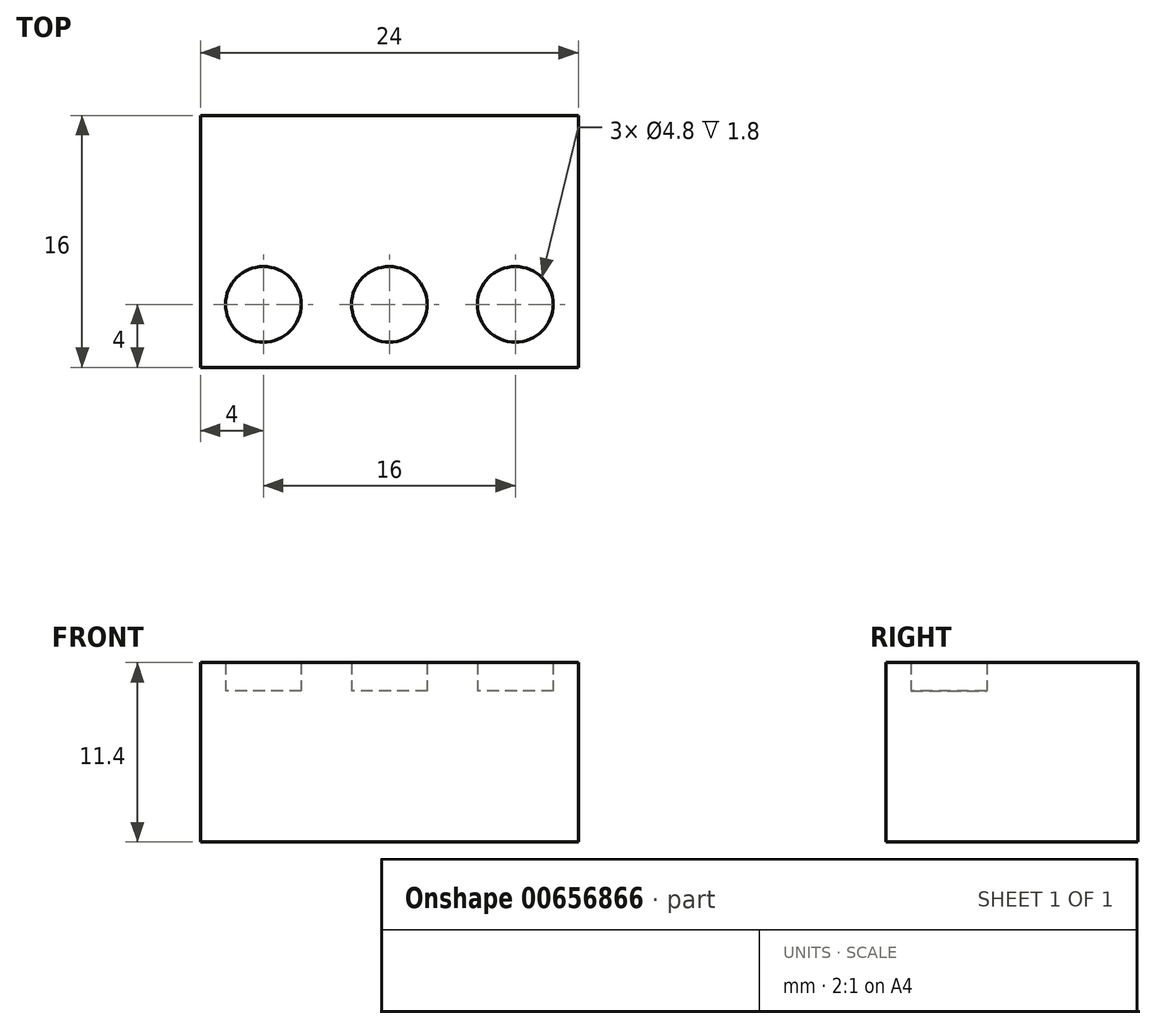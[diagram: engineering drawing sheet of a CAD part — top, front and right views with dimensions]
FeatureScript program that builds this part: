
annotation { "Feature Type Name" : "Feature", "Feature Type Description" : "" }
export const myFeature = defineFeature(function(context is Context, id is Id, definition is map)
    precondition{}
    {
        {
            var Q0;
            Q0=qCreatedBy(makeId("Top.planeOp"),FACE);
            var sketch = newSketch(context, id + "F0", { "sketchPlane" : qUnion([Q0])});
            skLineSegment(sketch, "E0.bottom", {"start": v(0, 0) * mm, "end": v(-24, 0) * mm});
            skLineSegment(sketch, "E0.top", {"start": v(0, 16) * mm, "end": v(-24, 16) * mm});
            skLineSegment(sketch, "E0.left", {"start": v(0, 0) * mm, "end": v(0, 16) * mm});
            skLineSegment(sketch, "E0.right", {"start": v(-24, 0) * mm, "end": v(-24, 16) * mm});
            skSolve(sketch);
        }
        {
            var Q0;
            Q0=makeQuery(id+"F0.imprint","IMPRINT",FACE,{"disambiguationData":[TD([[makeQuery(id+"F0.imprint","IMPRINT",EDGE,{"derivedFrom":sQuery(id+"F0.wireOp",EDGE,"E0.bottom")}),-1.0]])]});
            var Q1;
            Q1 = qSketchRegion(id + "F2", true);
            extrude(context, id + "F1", {"entities" : qUnion([Q0, Q1]), "depth" : 9.6 * mm, "offsetDistance" : 25.4 * mm});
        }
        {
            var Q0;
            Q0=makeQuery(id+"F1.opExtrude","CAP_FACE",FACE,{"disambiguationData":[OSD([sQuery(id+"F0.wireOp",EDGE,"E0.bottom"),sQuery(id+"F0.wireOp",EDGE,"E0.top"),sQuery(id+"F0.wireOp",EDGE,"E0.left"),sQuery(id+"F0.wireOp",EDGE,"E0.right")])],"isStart":false});
            var sketch = newSketch(context, id + "F2", { "sketchPlane" : qUnion([Q0])});
            skLineSegment(sketch, "E1", {"start": v(-24, 8) * mm, "end": v(0, 8) * mm, "construction": true});
            skLineSegment(sketch, "E2", {"start": v(-16, 16) * mm, "end": v(-16, 0) * mm, "construction": true});
            skLineSegment(sketch, "E3", {"start": v(-8, 16) * mm, "end": v(-8, 0) * mm, "construction": true});
            skLineSegment(sketch, "E4", {"start": v(-24, 16) * mm, "end": v(-16, 8) * mm, "construction": true});
            skLineSegment(sketch, "E5", {"start": v(-16, 8) * mm, "end": v(-8, 16) * mm, "construction": true});
            skLineSegment(sketch, "E6", {"start": v(-8, 16) * mm, "end": v(0, 8) * mm, "construction": true});
            skCircle(sketch, "E7", {"center": v(-20, 12) * mm, "radius": 2.4 * mm});
            skCircle(sketch, "E8", {"center": v(-12, 12) * mm, "radius": 2.4 * mm});
            skCircle(sketch, "E9", {"center": v(-4, 12) * mm, "radius": 2.4 * mm});
            skCircle(sketch, "E10.MirrorC", {"center": v(-20, 4) * mm, "radius": 2.4 * mm});
            skCircle(sketch, "E11.MirrorC", {"center": v(-12, 4) * mm, "radius": 2.4 * mm});
            skCircle(sketch, "E12.MirrorC", {"center": v(-4, 4) * mm, "radius": 2.4 * mm});
            skSolve(sketch);
        }
        {
            var Q0;
            Q0=makeQuery(id+"F2.imprint","IMPRINT",FACE,{"disambiguationData":[TD([[makeQuery(id+"F2.imprint","IMPRINT",EDGE,{"derivedFrom":sQuery(id+"F2.wireOp",EDGE,"E8")}),1.0]])]});
            var Q1;
            Q1=makeQuery(id+"F2.imprint","IMPRINT",FACE,{"disambiguationData":[TD([[makeQuery(id+"F2.imprint","IMPRINT",EDGE,{"derivedFrom":sQuery(id+"F2.wireOp",EDGE,"E9")}),1.0]])]});
            var Q2;
            Q2=makeQuery(id+"F2.imprint","IMPRINT",FACE,{"disambiguationData":[TD([[makeQuery(id+"F2.imprint","IMPRINT",EDGE,{"derivedFrom":sQuery(id+"F2.wireOp",EDGE,"E10.MirrorC")}),-1.0]])]});
            var Q3;
            Q3=makeQuery(id+"F2.imprint","IMPRINT",FACE,{"disambiguationData":[TD([[makeQuery(id+"F2.imprint","IMPRINT",EDGE,{"derivedFrom":sQuery(id+"F2.wireOp",EDGE,"E11.MirrorC")}),-1.0]])]});
            var Q4;
            Q4=makeQuery(id+"F2.imprint","IMPRINT",FACE,{"disambiguationData":[TD([[makeQuery(id+"F2.imprint","IMPRINT",EDGE,{"derivedFrom":sQuery(id+"F2.wireOp",EDGE,"E12.MirrorC")}),-1.0]])]});
            var Q5;
            Q5=makeQuery(id+"F2.imprint","IMPRINT",FACE,{"disambiguationData":[TD([[makeQuery(id+"F2.imprint","IMPRINT",EDGE,{"derivedFrom":sQuery(id+"F2.wireOp",EDGE,"E7")}),1.0]])]});
            extrude(context, id + "F3", {"entities" : qUnion([Q0, Q1, Q2, Q3, Q4, Q5]), "operationType" : NewBodyOperationType.ADD, "depth" : 1.8 * mm, "offsetDistance" : 25.4 * mm});
        }
    });
